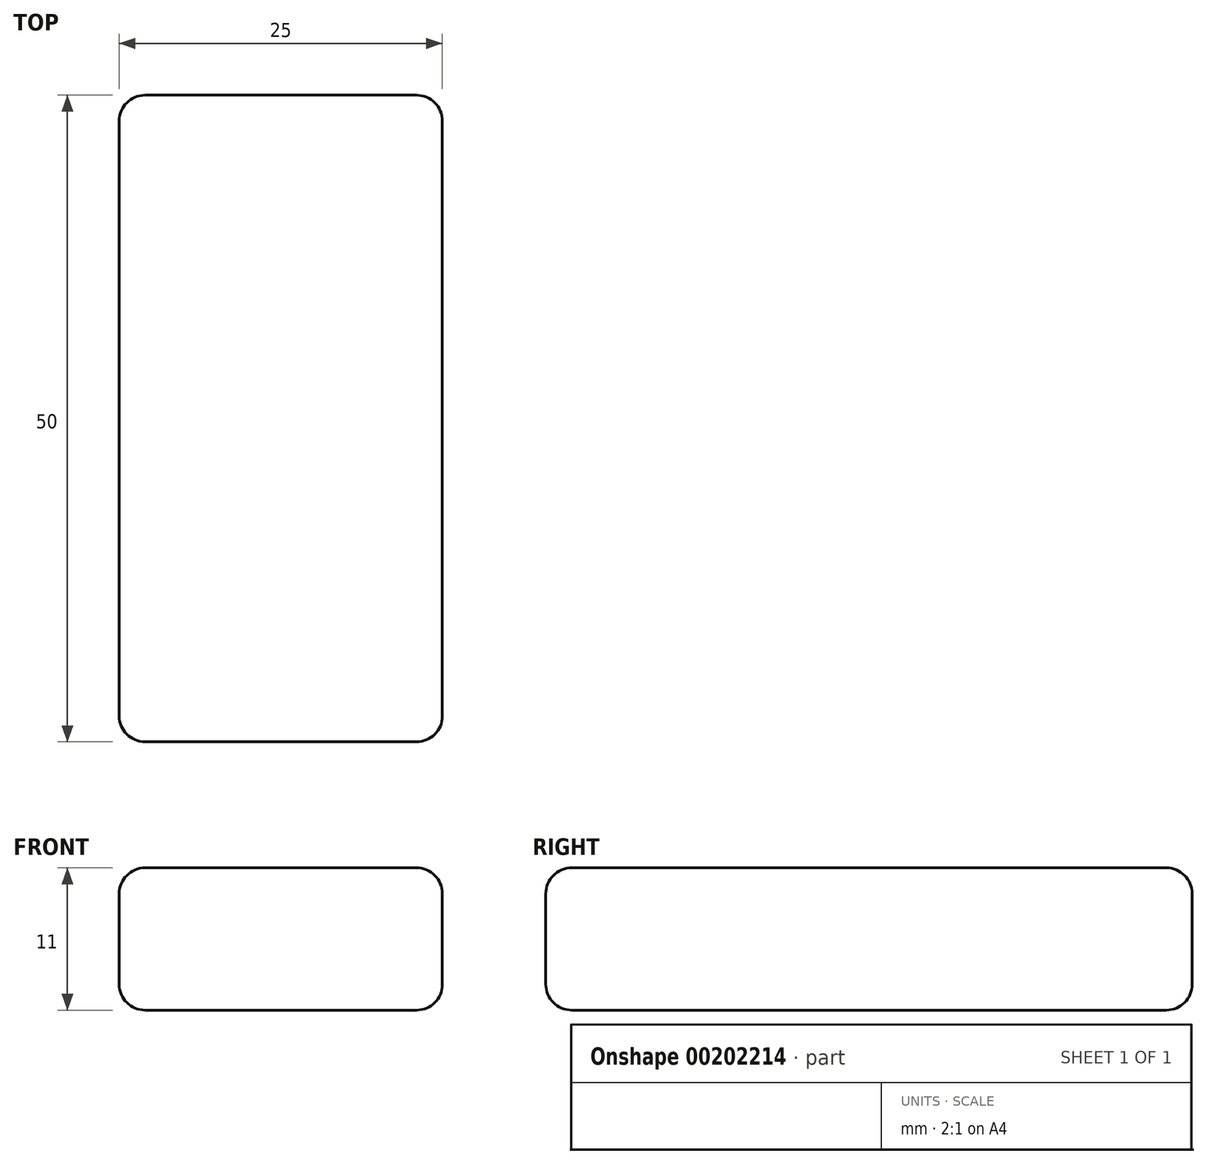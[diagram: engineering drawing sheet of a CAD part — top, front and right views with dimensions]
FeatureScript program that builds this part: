
annotation { "Feature Type Name" : "Feature", "Feature Type Description" : "" }
export const myFeature = defineFeature(function(context is Context, id is Id, definition is map)
    precondition{}
    {
        {
            var Q0;
            Q0=qCreatedBy(makeId("Top.planeOp"),FACE);
            var sketch = newSketch(context, id + "F0", { "sketchPlane" : qUnion([Q0])});
            skLineSegment(sketch, "E0.bottom", {"start": v(12.5, 25) * mm, "end": v(-12.5, 25) * mm});
            skLineSegment(sketch, "E0.top", {"start": v(12.5, -25) * mm, "end": v(-12.5, -25) * mm});
            skLineSegment(sketch, "E0.left", {"start": v(12.5, 25) * mm, "end": v(12.5, -25) * mm});
            skLineSegment(sketch, "E0.right", {"start": v(-12.5, 25) * mm, "end": v(-12.5, -25) * mm});
            skPoint(sketch, "E0.middle", {"position": v(0, 0) * mm});
            skSolve(sketch);
        }
        {
            var Q0;
            Q0=qSketchRegion(id+"F0",true);
            extrude(context, id + "F1", {"entities" : qUnion([Q0]), "depth" : 11 * mm});
        }
        {
            var Q0;
            Q0=makeQuery(id+"F1.opExtrude","CAP_FACE",FACE,{"disambiguationData":[OSD([sQuery(id+"F0.wireOp",EDGE,"E0.bottom"),sQuery(id+"F0.wireOp",EDGE,"E0.top"),sQuery(id+"F0.wireOp",EDGE,"E0.left"),sQuery(id+"F0.wireOp",EDGE,"E0.right")])],"isStart":false});
            var Q1;
            Q1=makeQuery(id+"F1.opExtrude","CAP_FACE",FACE,{"disambiguationData":[OSD([sQuery(id+"F0.wireOp",EDGE,"E0.bottom"),sQuery(id+"F0.wireOp",EDGE,"E0.top"),sQuery(id+"F0.wireOp",EDGE,"E0.left"),sQuery(id+"F0.wireOp",EDGE,"E0.right")])],"isStart":true});
            var Q2;
            Q2=makeQuery(id+"F1.opExtrude","SWEPT_FACE",FACE,{"disambiguationData":[OSD([sQuery(id+"F0.wireOp",EDGE,"E0.right")])]});
            var Q3;
            Q3=makeQuery(id+"F1.opExtrude","SWEPT_FACE",FACE,{"disambiguationData":[OSD([sQuery(id+"F0.wireOp",EDGE,"E0.left")])]});
            fillet(context, id + "F2", {"entities" : qUnion([Q0, Q1, Q2, Q3]), "radius" : 2 * mm, "tangentPropagation" : true, "allowEdgeOverflow" : false});
        }
    });
